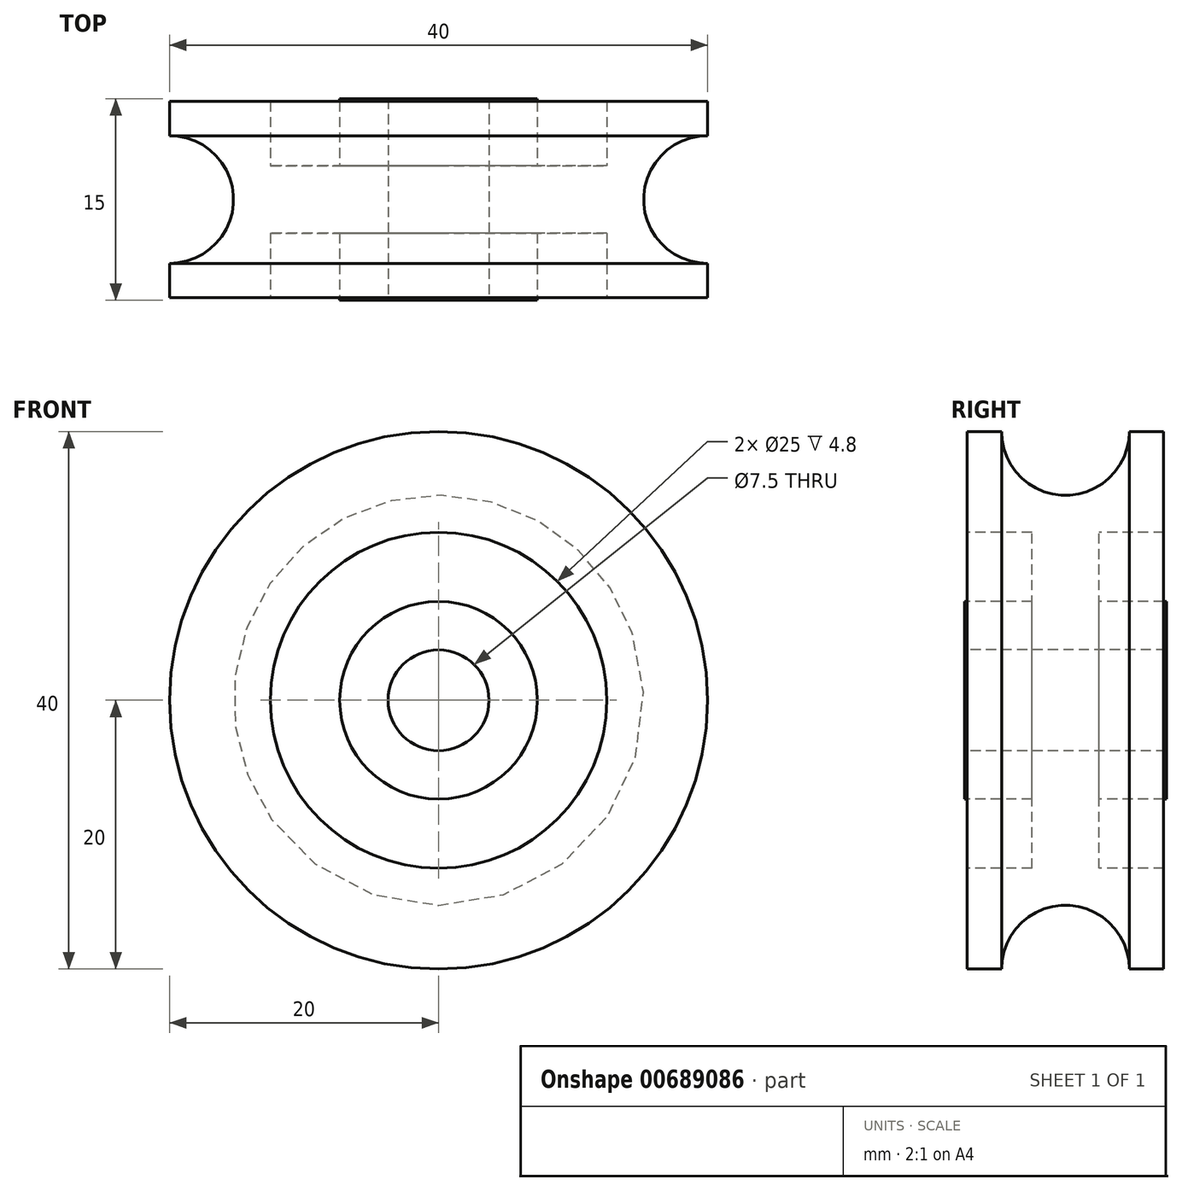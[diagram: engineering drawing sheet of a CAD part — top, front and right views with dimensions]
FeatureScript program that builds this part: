
annotation { "Feature Type Name" : "Feature", "Feature Type Description" : "" }
export const myFeature = defineFeature(function(context is Context, id is Id, definition is map)
    precondition{}
    {
        {
            var Q0;
            Q0=qCreatedBy(makeId("Right.planeOp"),FACE);
            var sketch = newSketch(context, id + "F0", { "sketchPlane" : qUnion([Q0])});
            skLineSegment(sketch, "E0", {"start": v(0, 0) * mm, "end": v(0, 20) * mm, "construction": true});
            skLineSegment(sketch, "E1", {"start": v(-7.5, 3.75) * mm, "end": v(7.5, 3.75) * mm});
            skLineSegment(sketch, "E2", {"start": v(7.5, 3.75) * mm, "end": v(7.5, 7.35) * mm});
            skLineSegment(sketch, "E3", {"start": v(7.5, 7.35) * mm, "end": v(2.5, 7.35) * mm});
            skLineSegment(sketch, "E4", {"start": v(2.5, 7.35) * mm, "end": v(2.5, 12.5) * mm});
            skLineSegment(sketch, "E5", {"start": v(2.5, 12.5) * mm, "end": v(7.3, 12.5) * mm});
            skLineSegment(sketch, "E6", {"start": v(7.3, 12.5) * mm, "end": v(7.3, 20) * mm});
            skLineSegment(sketch, "E7", {"start": v(7.3, 20) * mm, "end": v(4.75, 20) * mm});
            skLineSegment(sketch, "E8", {"start": v(-10.72, 0) * mm, "end": v(10.72, 0) * mm, "construction": true});
            skArc(sketch, "E9", {"start": v(4.75, 20) * mm, "mid": v(0, 15.25) * mm, "end": v(-4.75, 20) * mm});
            skLineSegment(sketch, "E10.MirrorCS", {"start": v(-7.3, 20) * mm, "end": v(-4.75, 20) * mm});
            skLineSegment(sketch, "E11.MirrorCS", {"start": v(-7.3, 12.5) * mm, "end": v(-7.3, 20) * mm});
            skLineSegment(sketch, "E12.MirrorCS", {"start": v(-7.5, 7.35) * mm, "end": v(-2.5, 7.35) * mm});
            skLineSegment(sketch, "E13.MirrorCS", {"start": v(-2.5, 7.35) * mm, "end": v(-2.5, 12.5) * mm});
            skLineSegment(sketch, "E14.MirrorCS", {"start": v(-2.5, 12.5) * mm, "end": v(-7.3, 12.5) * mm});
            skLineSegment(sketch, "E15.MirrorCS", {"start": v(-7.5, 3.75) * mm, "end": v(-7.5, 7.35) * mm});
            skSolve(sketch);
        }
        {
            var Q0;
            Q0=qSketchRegion(id+"F0",true);
            var Q1;
            Q1=sQuery(id+"F0.wireOp",EDGE,"E8");
            revolve(context, id + "F1", {"entities" : qUnion([Q0]), "axis" : qUnion([Q1]), "revolveType" : RevolveType.FULL});
        }
    });
